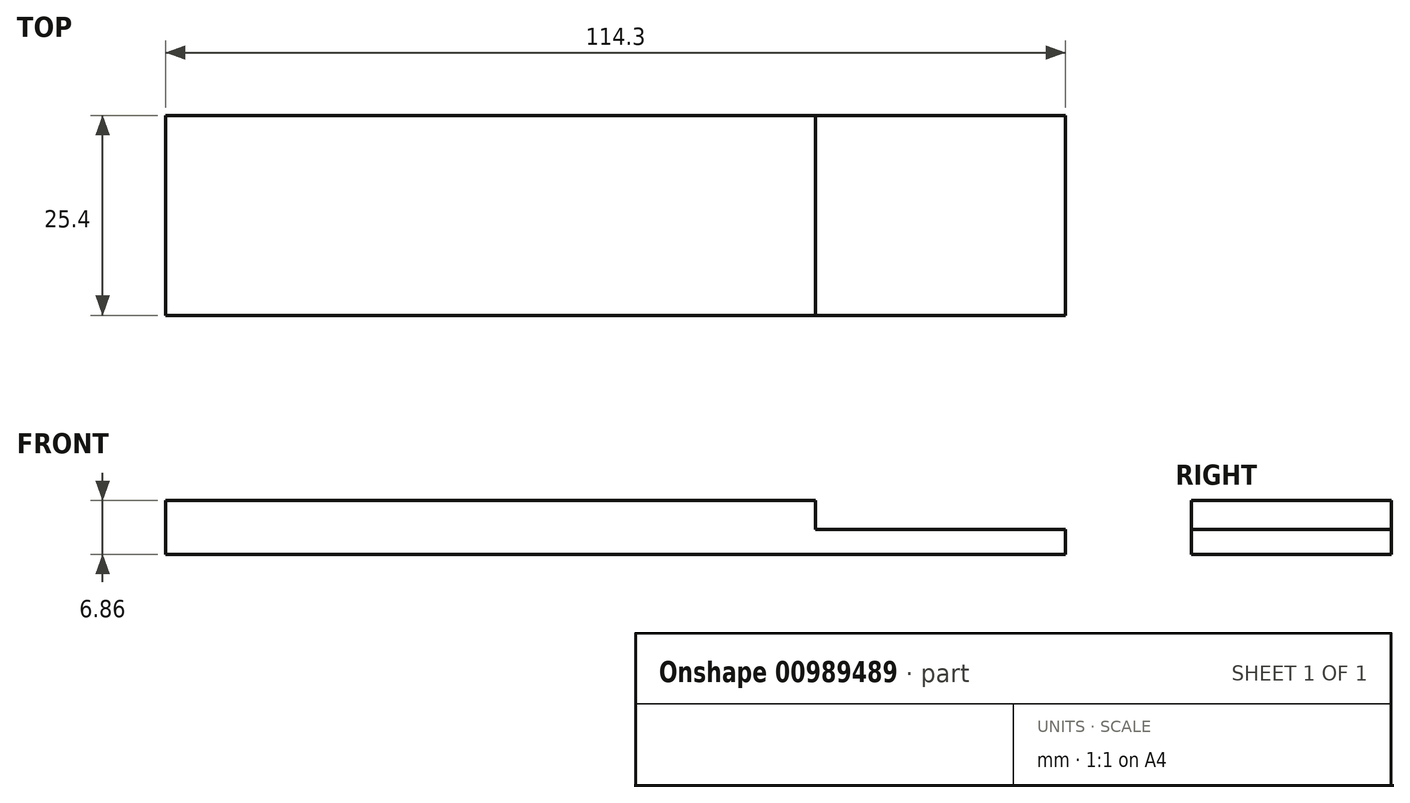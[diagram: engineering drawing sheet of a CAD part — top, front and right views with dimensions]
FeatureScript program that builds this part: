
annotation { "Feature Type Name" : "Feature", "Feature Type Description" : "" }
export const myFeature = defineFeature(function(context is Context, id is Id, definition is map)
    precondition{}
    {
        {
            var Q0;
            Q0=qCreatedBy(makeId("Front.planeOp"),FACE);
            var sketch = newSketch(context, id + "F0", { "sketchPlane" : qUnion([Q0])});
            skLineSegment(sketch, "E0", {"start": v(-41.28, 0) * mm, "end": v(73.03, 0) * mm});
            skLineSegment(sketch, "E1", {"start": v(73.03, 0) * mm, "end": v(73.03, 3.18) * mm});
            skLineSegment(sketch, "E2", {"start": v(73.03, 3.18) * mm, "end": v(41.28, 3.17) * mm});
            skLineSegment(sketch, "E3", {"start": v(41.28, 3.17) * mm, "end": v(41.28, 6.86) * mm});
            skLineSegment(sketch, "E4", {"start": v(-41.28, 0) * mm, "end": v(-41.28, 6.86) * mm});
            skLineSegment(sketch, "E5", {"start": v(-41.28, 6.86) * mm, "end": v(41.28, 6.86) * mm});
            skPoint(sketch, "E6", {"position": v(0, 6.86) * mm});
            skPoint(sketch, "E7", {"position": v(-41.28, 3.43) * mm});
            skSolve(sketch);
        }
        {
            var Q0;
            Q0=makeQuery(id+"F0.imprint","IMPRINT",FACE,{"disambiguationData":[TD([[makeQuery(id+"F0.imprint","IMPRINT",EDGE,{"derivedFrom":sQuery(id+"F0.wireOp",EDGE,"E0")}),1.0]])]});
            extrude(context, id + "F1", {"entities" : qUnion([Q0]), "depth" : 25.4 * mm, "offsetDistance" : 25.4 * mm});
        }
    });
